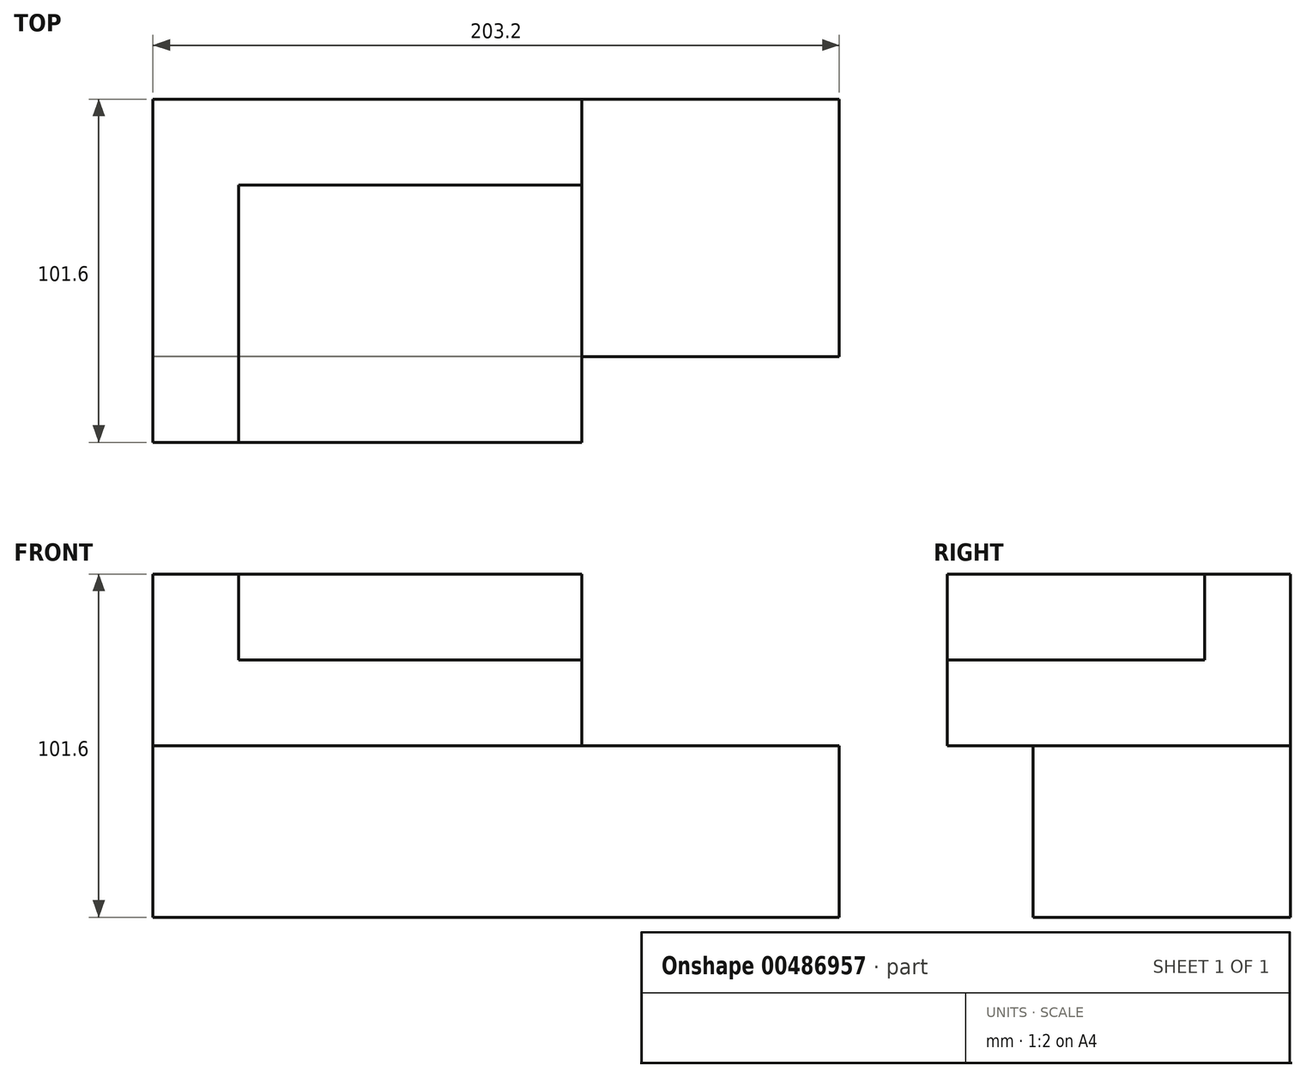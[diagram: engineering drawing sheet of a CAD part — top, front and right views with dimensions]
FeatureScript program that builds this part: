
annotation { "Feature Type Name" : "Feature", "Feature Type Description" : "" }
export const myFeature = defineFeature(function(context is Context, id is Id, definition is map)
    precondition{}
    {
        {
            var Q0;
            Q0=qCreatedBy(makeId("Right.planeOp"),FACE);
            var sketch = newSketch(context, id + "F0", { "sketchPlane" : qUnion([Q0])});
            skLineSegment(sketch, "E0.bottom", {"start": v(10.2, -56.95) * mm, "end": v(-66, -56.95) * mm});
            skLineSegment(sketch, "E0.left", {"start": v(10.2, -56.95) * mm, "end": v(10.2, -6.15) * mm});
            skLineSegment(sketch, "E0.right", {"start": v(-66, -56.95) * mm, "end": v(-66, -6.15) * mm});
            skLineSegment(sketch, "E1.bottom", {"start": v(-66, -6.15) * mm, "end": v(-91.4, -6.15) * mm});
            skLineSegment(sketch, "E1.top", {"start": v(10.2, 44.65) * mm, "end": v(-91.4, 44.65) * mm});
            skLineSegment(sketch, "E1.left", {"start": v(10.2, -6.15) * mm, "end": v(10.2, 44.65) * mm});
            skLineSegment(sketch, "E1.right", {"start": v(-91.4, -6.15) * mm, "end": v(-91.4, 44.65) * mm});
            skSolve(sketch);
        }
        {
            var Q0;
            Q0 = qSketchRegion(id + "F0", true);
            extrude(context, id + "F1", {"entities" : qUnion([Q0]), "depth" : 203.2 * mm});
        }
        {
            var Q0;
            Q0=makeQuery(id+"F1.opExtrude","SWEPT_FACE",FACE,{"disambiguationData":[OSD([sQuery(id+"F0.wireOp",EDGE,"E1.top")])]});
            var sketch = newSketch(context, id + "F2", { "sketchPlane" : qUnion([Q0])});
            skLineSegment(sketch, "E2.bottom", {"start": v(25.4, -91.4) * mm, "end": v(127, -91.4) * mm});
            skLineSegment(sketch, "E2.top", {"start": v(25.4, -15.2) * mm, "end": v(127, -15.2) * mm});
            skLineSegment(sketch, "E2.left", {"start": v(25.4, -91.4) * mm, "end": v(25.4, -15.2) * mm});
            skLineSegment(sketch, "E2.right", {"start": v(127, -91.4) * mm, "end": v(127, -15.2) * mm});
            skSolve(sketch);
        }
        {
            var Q0;
            Q0 = qSketchRegion(id + "F2", true);
            var Q1;
            Q1=makeQuery(id+"F2.imprint","IMPRINT",FACE,{"disambiguationData":[TD([[makeQuery(id+"F2.imprint","IMPRINT",EDGE,{"derivedFrom":sQuery(id+"F2.wireOp",EDGE,"E2.bottom")}),-1.0]])]});
            extrude(context, id + "F3", {"entities" : qUnion([Q0, Q1]), "operationType" : NewBodyOperationType.REMOVE, "oppositeDirection" : true, "depth" : 25.4 * mm});
        }
        {
            var Q0;
            Q0=makeQuery(id+"F1.opExtrude","SWEPT_FACE",FACE,{"disambiguationData":[OSD([sQuery(id+"F0.wireOp",EDGE,"E1.top")])]});
            var sketch = newSketch(context, id + "F4", { "sketchPlane" : qUnion([Q0])});
            skLineSegment(sketch, "E3.bottom", {"start": v(203.2, 10.2) * mm, "end": v(127, 10.2) * mm});
            skLineSegment(sketch, "E3.top", {"start": v(203.2, -91.4) * mm, "end": v(127, -91.4) * mm});
            skLineSegment(sketch, "E3.left", {"start": v(203.2, 10.2) * mm, "end": v(203.2, -91.4) * mm});
            skLineSegment(sketch, "E3.right", {"start": v(127, 10.2) * mm, "end": v(127, -91.4) * mm});
            skSolve(sketch);
        }
        {
            var Q0;
            {var subQ2=sQuery(id+"F4.wireOp",EDGE,"E3.bottom");Q0=makeQuery(id+"F4.imprint","IMPRINT",FACE,{"disambiguationData":[TD([[makeQuery(id+"F4.imprint","IMPRINT",EDGE,{"derivedFrom":subQ2}),1.0]])]});}
            extrude(context, id + "F5", {"entities" : qUnion([Q0]), "operationType" : NewBodyOperationType.REMOVE, "oppositeDirection" : true, "depth" : 50.8 * mm});
        }
    });
